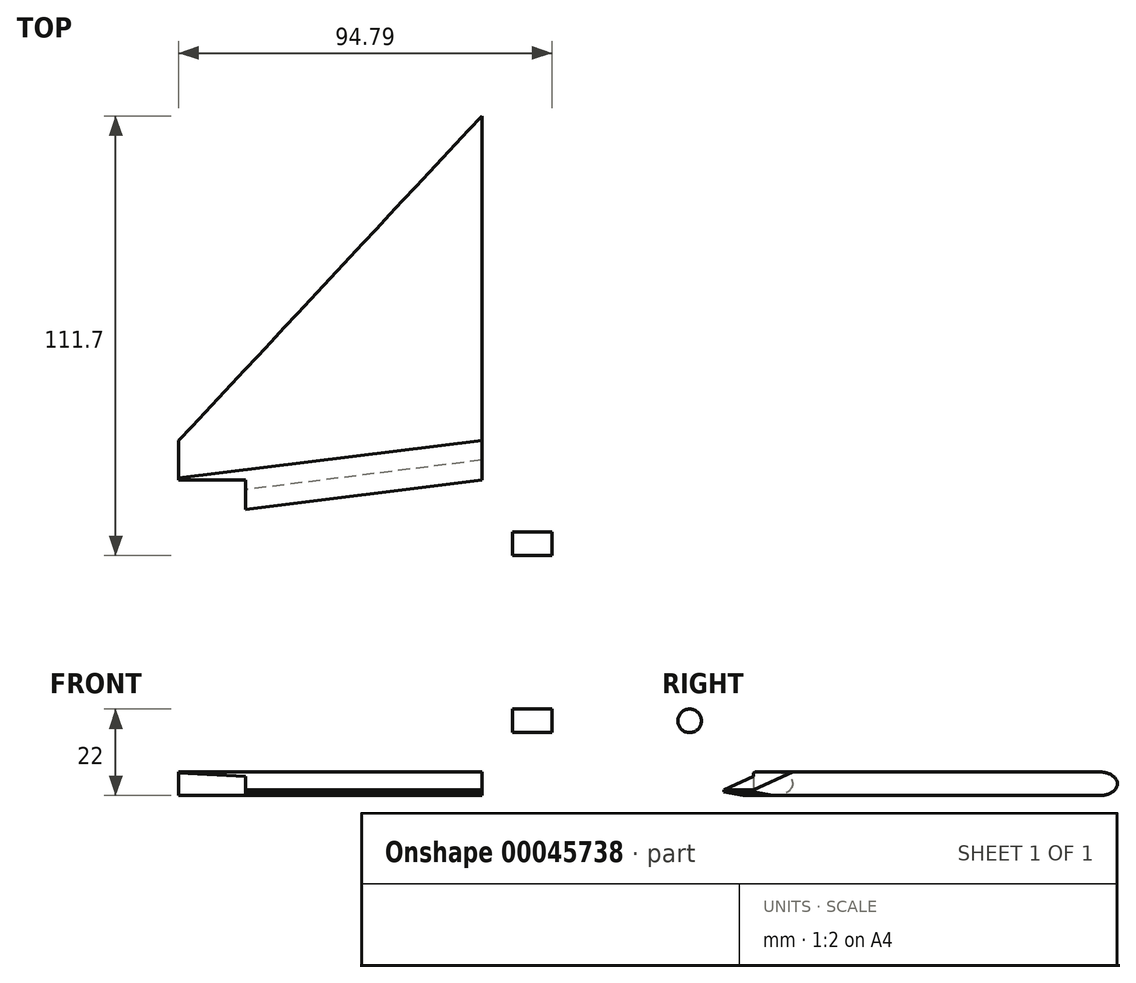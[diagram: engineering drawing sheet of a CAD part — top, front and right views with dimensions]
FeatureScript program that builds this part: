
annotation { "Feature Type Name" : "Feature", "Feature Type Description" : "" }
export const myFeature = defineFeature(function(context is Context, id is Id, definition is map)
    precondition{}
    {
        {
            var Q0;
            Q0=qCreatedBy(makeId("Top.planeOp"),FACE);
            var sketch = newSketch(context, id + "F0", { "sketchPlane" : qUnion([Q0])});
            skLineSegment(sketch, "E0", {"start": v(-42.21, 66.88) * mm, "end": v(-42.21, -8.12) * mm});
            skLineSegment(sketch, "E1", {"start": v(-42.21, -8.12) * mm, "end": v(27.79, -8.12) * mm});
            skLineSegment(sketch, "E2", {"start": v(-42.21, 66.88) * mm, "end": v(27.79, -8.13) * mm});
            skLineSegment(sketch, "E3", {"start": v(-42.21, -8.12) * mm, "end": v(-42.21, -18.12) * mm});
            skLineSegment(sketch, "E4", {"start": v(-42.21, -18.12) * mm, "end": v(27.79, -18.12) * mm});
            skLineSegment(sketch, "E5", {"start": v(27.79, -18.12) * mm, "end": v(17.79, -18.12) * mm});
            skLineSegment(sketch, "E6", {"start": v(17.79, -18.12) * mm, "end": v(17.79, -25.62) * mm});
            skLineSegment(sketch, "E7", {"start": v(17.79, -25.62) * mm, "end": v(-42.21, -18.12) * mm});
            skLineSegment(sketch, "E8", {"start": v(-42.21, 66.88) * mm, "end": v(-42.21, 74.38) * mm});
            skLineSegment(sketch, "E9", {"start": v(27.79, -8.12) * mm, "end": v(34.79, -8.12) * mm});
            skLineSegment(sketch, "E10", {"start": v(27.79, -18.12) * mm, "end": v(34.79, -18.12) * mm});
            skLineSegment(sketch, "E11", {"start": v(34.79, -8.12) * mm, "end": v(34.79, -18.12) * mm});
            skLineSegment(sketch, "E12", {"start": v(-42.21, 74.38) * mm, "end": v(34.79, -8.13) * mm});
            skLineSegment(sketch, "E13", {"start": v(34.79, -18.12) * mm, "end": v(17.79, -25.62) * mm});
            skSolve(sketch);
        }
        {
            var Q0;
            Q0=makeQuery(id+"F0.imprint","IMPRINT",FACE,{"disambiguationData":[TD([[makeQuery(id+"F0.imprint","IMPRINT",EDGE,{"derivedFrom":sQuery(id+"F0.wireOp",EDGE,"E2")}),1.0]])]});
            var Q1;
            Q1=makeQuery(id+"F0.imprint","IMPRINT",FACE,{"disambiguationData":[TD([[makeQuery(id+"F0.imprint","IMPRINT",EDGE,{"derivedFrom":sQuery(id+"F0.wireOp",EDGE,"E0")}),1.0]])]});
            var Q2;
            Q2=makeQuery(id+"F0.imprint","IMPRINT",FACE,{"disambiguationData":[TD([[makeQuery(id+"F0.imprint","IMPRINT",EDGE,{"derivedFrom":sQuery(id+"F0.wireOp",EDGE,"E1")}),-1.0]])]});
            var Q3;
            Q3=makeQuery(id+"F0.imprint","IMPRINT",FACE,{"disambiguationData":[TD([[makeQuery(id+"F0.imprint","IMPRINT",EDGE,{"derivedFrom":sQuery(id+"F0.wireOp",EDGE,"E4")}),-1.0]])]});
            var Q4;
            Q4=makeQuery(id+"F0.imprint","IMPRINT",FACE,{"disambiguationData":[TD([[makeQuery(id+"F0.imprint","IMPRINT",EDGE,{"derivedFrom":sQuery(id+"F0.wireOp",EDGE,"E5")}),1.0]])]});
            extrude(context, id + "F1", {"entities" : qUnion([Q0, Q1, Q2, Q3, Q4]), "depth" : 6 * mm});
        }
        {
            var Q0;
            Q0=makeQuery(id+"F1.opExtrude","SWEPT_BODY",BODY,{"disambiguationData":[OSD([sQuery(id+"F0.wireOp",EDGE,"E0"),sQuery(id+"F0.wireOp",EDGE,"E3"),sQuery(id+"F0.wireOp",EDGE,"E7"),sQuery(id+"F0.wireOp",EDGE,"E8"),sQuery(id+"F0.wireOp",EDGE,"E11"),sQuery(id+"F0.wireOp",EDGE,"E12"),sQuery(id+"F0.wireOp",EDGE,"E13")])]});
            var Q1;
            Q1=qCreatedBy(makeId("Right.planeOp"),FACE);
            transform(context, id + "F2", {"entities" : qUnion([Q0]), "transformType" : TransformType.TRANSLATION_DISTANCE, "transformDirection" : qUnion([Q1]), "distance" : 50 * mm, "makeCopy" : false});
        }
        {
            var Q0;
            Q0=makeQuery(id+"F1.opExtrude","SWEPT_BODY",BODY,{"disambiguationData":[OSD([sQuery(id+"F0.wireOp",EDGE,"E0"),sQuery(id+"F0.wireOp",EDGE,"E3"),sQuery(id+"F0.wireOp",EDGE,"E7"),sQuery(id+"F0.wireOp",EDGE,"E8"),sQuery(id+"F0.wireOp",EDGE,"E11"),sQuery(id+"F0.wireOp",EDGE,"E12"),sQuery(id+"F0.wireOp",EDGE,"E13")])]});
            var Q1;
            Q1=qCreatedBy(makeId("Right.planeOp"),FACE);
            mirror(context, id + "F3", {"entities" : qUnion([Q0]), "mirrorPlane" : qUnion([Q1])});
        }
        {
            var Q0;
            Q0=makeQuery(id+"F1.opExtrude","SWEPT_BODY",BODY,{"disambiguationData":[OSD([sQuery(id+"F0.wireOp",EDGE,"E0"),sQuery(id+"F0.wireOp",EDGE,"E3"),sQuery(id+"F0.wireOp",EDGE,"E7"),sQuery(id+"F0.wireOp",EDGE,"E8"),sQuery(id+"F0.wireOp",EDGE,"E11"),sQuery(id+"F0.wireOp",EDGE,"E12"),sQuery(id+"F0.wireOp",EDGE,"E13")])]});
            deleteBodies(context, id + "F4", {"entities" : qUnion([Q0])});
        }
        {
            var Q0;
            Q0=makeQuery(id+"F3.opPattern","COPY",EDGE,{"derivedFrom":makeQuery(id+"F1.opExtrude","CAP_EDGE",EDGE,{"disambiguationData":[OSD([sQuery(id+"F0.wireOp",EDGE,"E12")])],"isStart":false}),"instanceName":"1"});
            var Q1;
            Q1=makeQuery(id+"F3.opPattern","COPY",EDGE,{"derivedFrom":makeQuery(id+"F1.opExtrude","CAP_EDGE",EDGE,{"disambiguationData":[OSD([sQuery(id+"F0.wireOp",EDGE,"E12")])],"isStart":true}),"instanceName":"1"});
            fillet(context, id + "F5", {"entities" : qUnion([Q0, Q1]), "radius" : 3 * mm, "tangentPropagation" : true, "rho" : .4, "crossSection" : FilletCrossSection.CONIC, "allowEdgeOverflow" : false});
        }
        {
            var Q0;
            Q0=makeQuery(id+"F3.opPattern","COPY",EDGE,{"derivedFrom":makeQuery(id+"F1.opExtrude","CAP_EDGE",EDGE,{"disambiguationData":[OSD([sQuery(id+"F0.wireOp",EDGE,"E7")])],"isStart":false}),"instanceName":"1"});
            var Q1;
            Q1=makeQuery(id+"F3.opPattern","COPY",EDGE,{"derivedFrom":makeQuery(id+"F1.opExtrude","CAP_EDGE",EDGE,{"disambiguationData":[OSD([sQuery(id+"F0.wireOp",EDGE,"E13")])],"isStart":false}),"instanceName":"1"});
            chamfer(context, id + "F6", {"entities" : qUnion([Q0, Q1]), "chamferType" : ChamferType.TWO_OFFSETS, "width1" : 4.5 * mm, "oppositeDirection" : true, "width2" : 10 * mm, "tangentPropagation" : true});
        }
        {
            var Q0;
            Q0=makeQuery(id+"F3.opPattern","COPY",EDGE,{"derivedFrom":makeQuery(id+"F1.opExtrude","CAP_EDGE",EDGE,{"disambiguationData":[OSD([sQuery(id+"F0.wireOp",EDGE,"E7")])],"isStart":true}),"instanceName":"1"});
            var Q1;
            Q1=makeQuery(id+"F3.opPattern","COPY",EDGE,{"derivedFrom":makeQuery(id+"F1.opExtrude","CAP_EDGE",EDGE,{"disambiguationData":[OSD([sQuery(id+"F0.wireOp",EDGE,"E13")])],"isStart":true}),"instanceName":"1"});
            chamfer(context, id + "F7", {"entities" : qUnion([Q0, Q1]), "chamferType" : ChamferType.TWO_OFFSETS, "width1" : 5 * mm, "oppositeDirection" : true, "width2" : 1 * mm, "tangentPropagation" : true});
        }
        {
            var Q0;
            Q0=qCreatedBy(makeId("Right.planeOp"),FACE);
            var sketch = newSketch(context, id + "F8", { "sketchPlane" : qUnion([Q0])});
            skCircle(sketch, "E14", {"center": v(-34.32, 19) * mm, "radius": 3 * mm});
            skCircle(sketch, "E15", {"center": v(-21.44, 41.35) * mm, "radius": 3.3 * mm});
            skSolve(sketch);
        }
        {
            var Q0;
            Q0=makeQuery(id+"F8.imprint","IMPRINT",FACE,{"disambiguationData":[TD([[makeQuery(id+"F8.imprint","IMPRINT",EDGE,{"derivedFrom":sQuery(id+"F8.wireOp",EDGE,"E14")}),1.0]])]});
            extrude(context, id + "F9", {"entities" : qUnion([Q0]), "depth" : 10 * mm});
        }
    });
